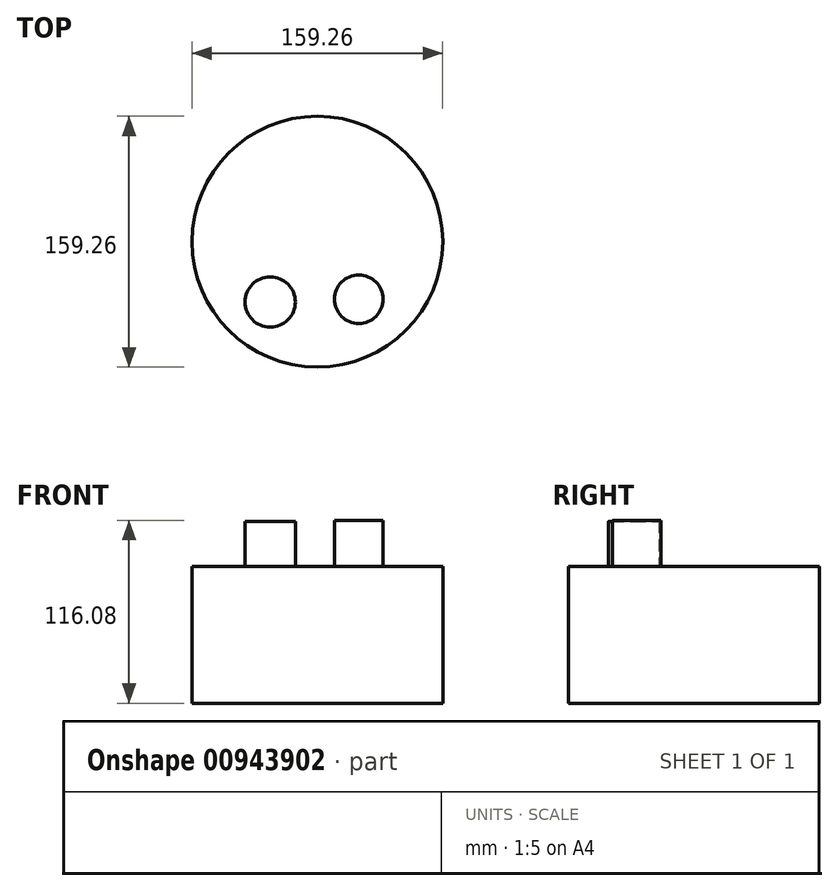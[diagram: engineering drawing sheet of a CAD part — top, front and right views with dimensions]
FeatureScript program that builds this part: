
annotation { "Feature Type Name" : "Feature", "Feature Type Description" : "" }
export const myFeature = defineFeature(function(context is Context, id is Id, definition is map)
    precondition{}
    {
        {
            var Q0;
            Q0=qCreatedBy(makeId("Top.planeOp"),FACE);
            var sketch = newSketch(context, id + "F0", { "sketchPlane" : qUnion([Q0])});
            skCircle(sketch, "E0", {"center": v(0, 0) * mm, "radius": 79.63 * mm});
            skSolve(sketch);
        }
        {
            var Q0;
            Q0=makeQuery(id+"F0.imprint","IMPRINT",FACE,{"disambiguationData":[TD([[makeQuery(id+"F0.imprint","IMPRINT",EDGE,{"derivedFrom":sQuery(id+"F0.wireOp",EDGE,"E0")}),1.0]])]});
            var sketch = newSketch(context, id + "F1", { "sketchPlane" : qUnion([Q0])});
            skCircle(sketch, "E1", {"center": v(-29.93, -38.35) * mm, "radius": 15.93 * mm});
            skSolve(sketch);
        }
        {
            var Q0;
            Q0=makeQuery(id+"F1.imprint","IMPRINT",FACE,{"disambiguationData":[TD([[makeQuery(id+"F1.imprint","IMPRINT",EDGE,{"derivedFrom":sQuery(id+"F1.wireOp",EDGE,"E1")}),-1.0]])]});
            var sketch = newSketch(context, id + "F2", { "sketchPlane" : qUnion([Q0])});
            skCircle(sketch, "E2", {"center": v(26.32, -36.55) * mm, "radius": 15.42 * mm});
            skSolve(sketch);
        }
        {
            var Q0;
            Q0=qCreatedBy(makeId("Top.planeOp"),FACE);
            var sketch = newSketch(context, id + "F3", { "sketchPlane" : qUnion([Q0])});
            skArc(sketch, "E3", {"start": v(37.91, 45.67) * mm, "mid": v(-0.34, 54.85) * mm, "end": v(-38.21, 44.22) * mm});
            skSolve(sketch);
        }
        {
            var Q0;
            Q0=qCreatedBy(makeId("Top.planeOp"),FACE);
            var sketch = newSketch(context, id + "F4", { "sketchPlane" : qUnion([Q0])});
            skArc(sketch, "E4", {"start": v(30.65, 66.3) * mm, "mid": v(-7.97, 69.3) * mm, "end": v(-38.21, 45.09) * mm});
            skSolve(sketch);
        }
        {
            var Q0;
            Q0=qCreatedBy(makeId("Top.planeOp"),FACE);
            var sketch = newSketch(context, id + "F5", { "sketchPlane" : qUnion([Q0])});
            skLineSegment(sketch, "E5", {"start": v(30.65, 66) * mm, "end": v(37.33, 45.38) * mm});
            skSolve(sketch);
        }
        {
            var Q0;
            Q0=makeQuery(id+"F0.imprint","IMPRINT",FACE,{"disambiguationData":[TD([[makeQuery(id+"F0.imprint","IMPRINT",EDGE,{"derivedFrom":sQuery(id+"F0.wireOp",EDGE,"E0")}),1.0]])]});
            extrude(context, id + "F6", {"entities" : qUnion([Q0]), "depth" : 86.87 * mm, "offsetDistance" : 25.4 * mm});
        }
        {
            var Q0;
            Q0=makeQuery(id+"F2.imprint","IMPRINT",FACE,{"disambiguationData":[TD([[makeQuery(id+"F2.imprint","IMPRINT",EDGE,{"derivedFrom":makeQuery(id+"F1.imprint","IMPRINT",EDGE,{"derivedFrom":sQuery(id+"F1.wireOp",EDGE,"E1")})}),1.0]])]});
            extrude(context, id + "F7", {"entities" : qUnion([Q0]), "operationType" : NewBodyOperationType.ADD, "depth" : 115.57 * mm, "offsetDistance" : 25.4 * mm});
        }
        {
            var Q0;
            Q0=makeQuery(id+"F2.imprint","IMPRINT",FACE,{"disambiguationData":[TD([[makeQuery(id+"F2.imprint","IMPRINT",EDGE,{"derivedFrom":sQuery(id+"F2.wireOp",EDGE,"E2")}),1.0]])]});
            extrude(context, id + "F8", {"entities" : qUnion([Q0]), "operationType" : NewBodyOperationType.ADD, "depth" : 116.08 * mm, "offsetDistance" : 25.4 * mm});
        }
        {
            var Q0;
            Q0 = qSketchRegion(id + "F4", true);
            var Q1;
            Q1 = qSketchRegion(id + "F3", true);
            var Q2;
            Q2 = qSketchRegion(id + "F5", true);
            var Q3;
            Q3=makeQuery(id+"F2.imprint","IMPRINT",FACE,{"disambiguationData":[TD([[makeQuery(id+"F2.imprint","IMPRINT",EDGE,{"derivedFrom":sQuery(id+"F2.wireOp",EDGE,"E2")}),-1.0]])]});
            extrude(context, id + "F9", {"entities" : qUnion([Q0, Q1, Q2, Q3]), "operationType" : NewBodyOperationType.ADD, "depth" : 46.74 * mm, "offsetDistance" : 25.4 * mm});
        }
    });
